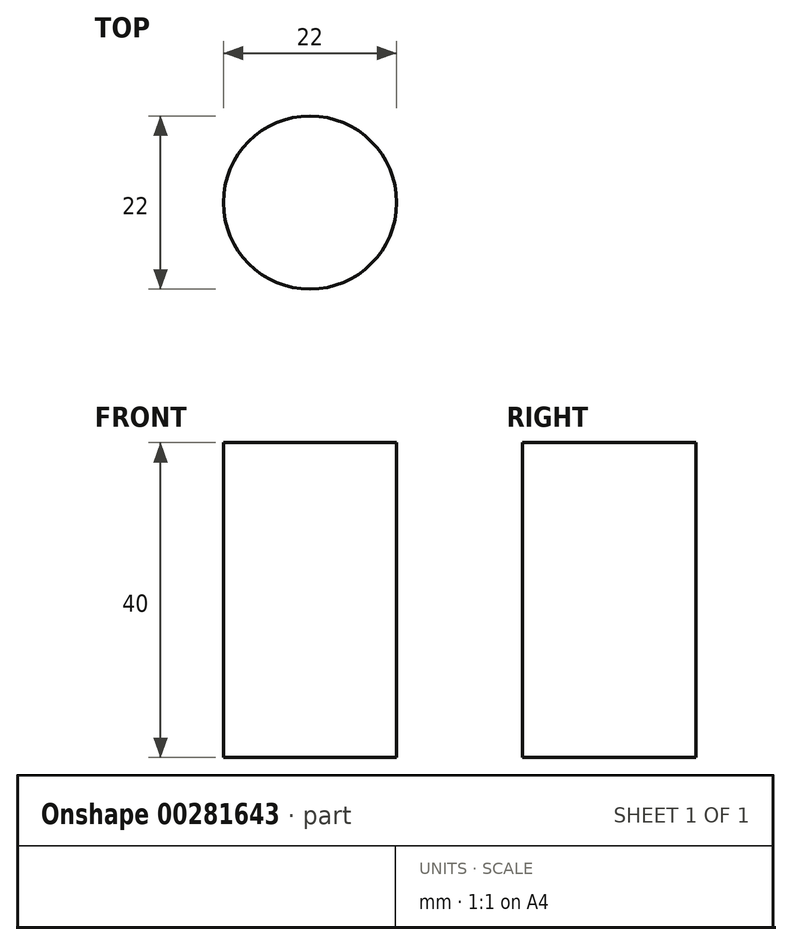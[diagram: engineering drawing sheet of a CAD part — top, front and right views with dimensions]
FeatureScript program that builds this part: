
annotation { "Feature Type Name" : "Feature", "Feature Type Description" : "" }
export const myFeature = defineFeature(function(context is Context, id is Id, definition is map)
    precondition{}
    {
        {
            var Q0;
            Q0=qCreatedBy(makeId("Top.planeOp"),FACE);
            var sketch = newSketch(context, id + "F0", { "sketchPlane" : qUnion([Q0])});
            skCircle(sketch, "E0", {"center": v(0, 0) * mm, "radius": 11 * mm});
            skSolve(sketch);
        }
        {
            var Q0;
            Q0=makeQuery(id+"F0.imprint","IMPRINT",FACE,{"disambiguationData":[TD([[makeQuery(id+"F0.imprint","IMPRINT",EDGE,{"derivedFrom":sQuery(id+"F0.wireOp",EDGE,"E0")}),1.0]])]});
            extrude(context, id + "F1", {"entities" : qUnion([Q0]), "depth" : 40 * mm, "offsetDistance" : 25 * mm});
        }
    });
